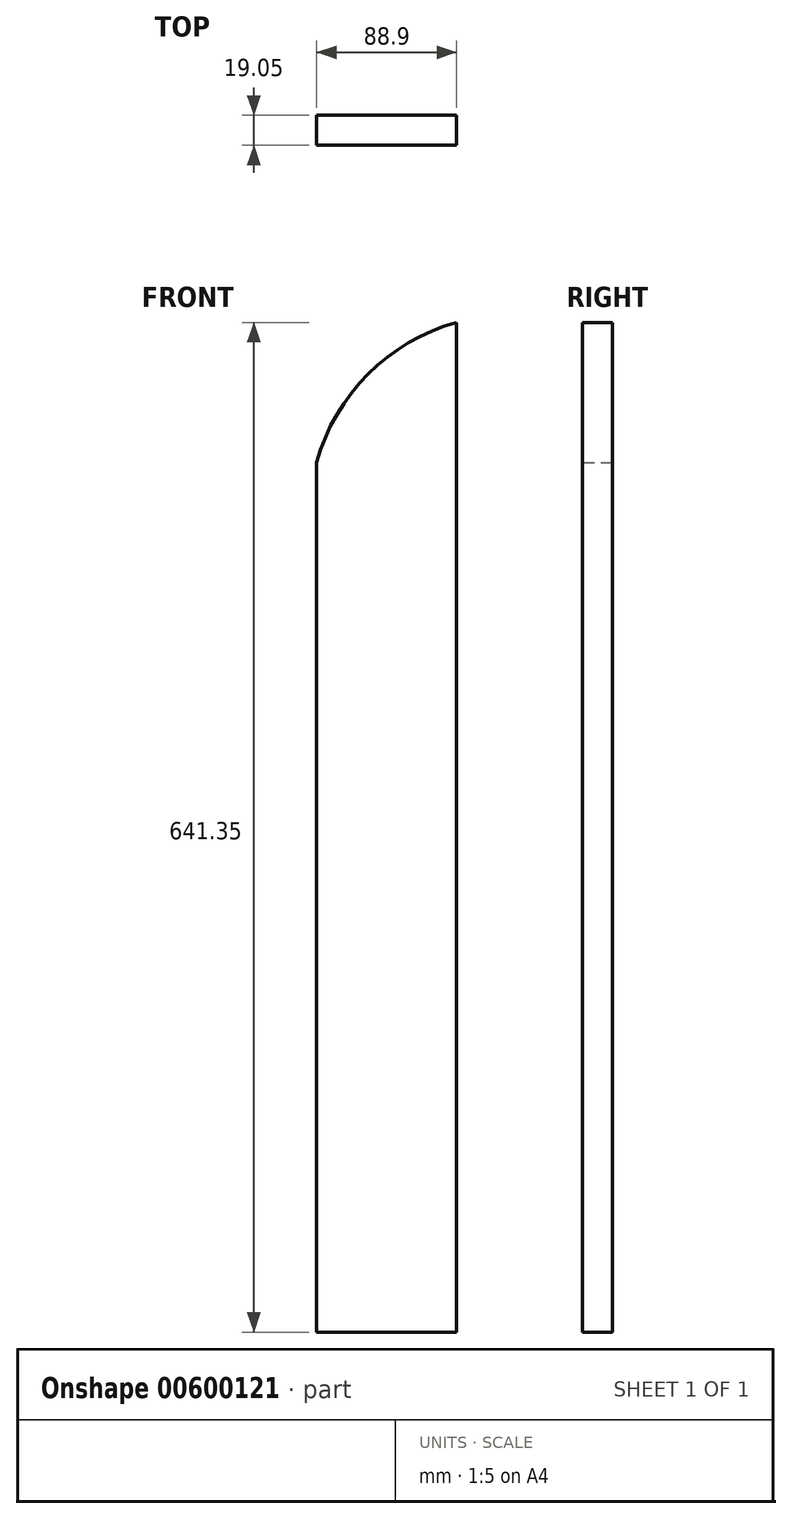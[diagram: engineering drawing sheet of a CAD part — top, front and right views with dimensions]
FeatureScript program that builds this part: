
annotation { "Feature Type Name" : "Feature", "Feature Type Description" : "" }
export const myFeature = defineFeature(function(context is Context, id is Id, definition is map)
    precondition{}
    {
        {
            var Q0;
            Q0=qCreatedBy(makeId("Front.planeOp"),FACE);
            var sketch = newSketch(context, id + "F0", { "sketchPlane" : qUnion([Q0])});
            skLineSegment(sketch, "E0.bottom", {"start": v(0, 0) * mm, "end": v(-88.9, 0) * mm});
            skLineSegment(sketch, "E0.top", {"start": v(0, 641.35) * mm, "end": v(-88.9, 641.35) * mm, "construction": true});
            skLineSegment(sketch, "E0.left", {"start": v(0, 0) * mm, "end": v(0, 641.35) * mm});
            skLineSegment(sketch, "E0.right", {"start": v(-88.9, 0) * mm, "end": v(-88.9, 641.35) * mm, "construction": true});
            skLineSegment(sketch, "E1", {"start": v(-88.9, 0) * mm, "end": v(-88.9, 552.45) * mm});
            skArc(sketch, "E2", {"start": v(0, 641.35) * mm, "mid": v(-56.22, 608.67) * mm, "end": v(-88.9, 552.45) * mm});
            skSolve(sketch);
        }
        {
            var Q0;
            Q0 = qSketchRegion(id + "F0", true);
            extrude(context, id + "F1", {"entities" : qUnion([Q0]), "depth" : 19.05 * mm, "offsetDistance" : 25.4 * mm});
        }
    });
